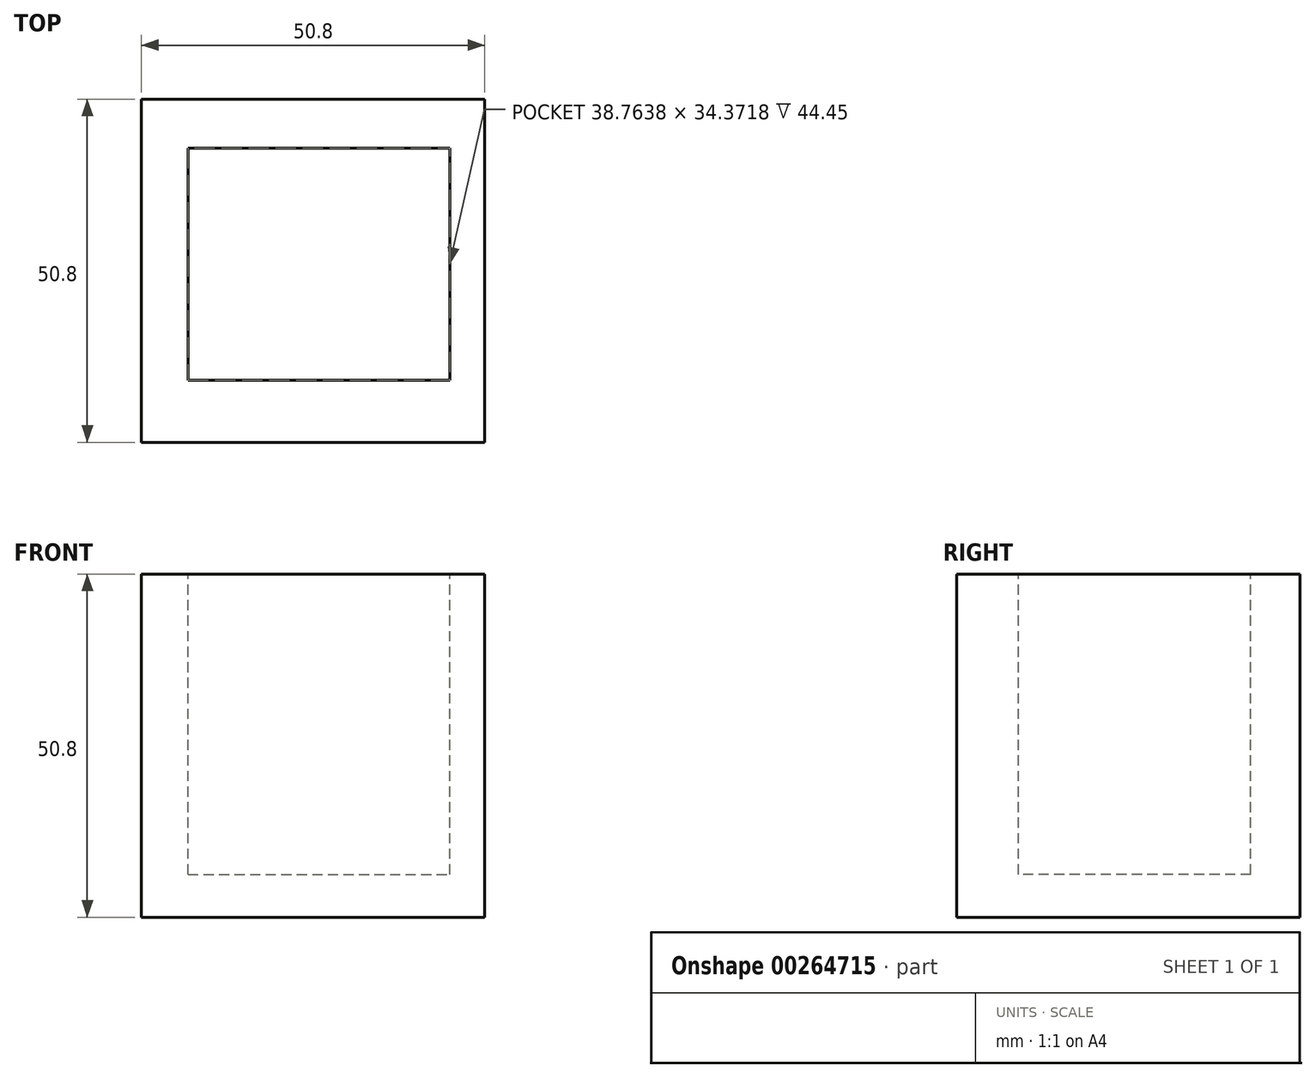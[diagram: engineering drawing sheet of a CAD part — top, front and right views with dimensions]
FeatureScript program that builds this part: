
annotation { "Feature Type Name" : "Feature", "Feature Type Description" : "" }
export const myFeature = defineFeature(function(context is Context, id is Id, definition is map)
    precondition{}
    {
        {
            var Q0;
            Q0=qCreatedBy(makeId("Front.planeOp"),FACE);
            var sketch = newSketch(context, id + "F0", { "sketchPlane" : qUnion([Q0])});
            skLineSegment(sketch, "E0.bottom", {"start": v(0, 0) * mm, "end": v(-50.8, 0) * mm});
            skLineSegment(sketch, "E0.top", {"start": v(0, 50.8) * mm, "end": v(-50.8, 50.8) * mm});
            skLineSegment(sketch, "E0.left", {"start": v(0, 0) * mm, "end": v(0, 50.8) * mm});
            skLineSegment(sketch, "E0.right", {"start": v(-50.8, 0) * mm, "end": v(-50.8, 50.8) * mm});
            skSolve(sketch);
        }
        {
            var Q0;
            Q0 = qSketchRegion(id + "F0", true);
            extrude(context, id + "F1", {"entities" : qUnion([Q0]), "depth" : 50.8 * mm});
        }
        {
            var Q0;
            Q0=makeQuery(id+"F1.opExtrude","SWEPT_FACE",FACE,{"disambiguationData":[OSD([sQuery(id+"F0.wireOp",EDGE,"E0.top")])]});
            var sketch = newSketch(context, id + "F2", { "sketchPlane" : qUnion([Q0])});
            skLineSegment(sketch, "E1.bottom", {"start": v(-43.92, -7.26) * mm, "end": v(-5.16, -7.26) * mm});
            skLineSegment(sketch, "E1.top", {"start": v(-43.92, -41.63) * mm, "end": v(-5.16, -41.63) * mm});
            skLineSegment(sketch, "E1.left", {"start": v(-43.92, -7.26) * mm, "end": v(-43.92, -41.63) * mm});
            skLineSegment(sketch, "E1.right", {"start": v(-5.16, -7.26) * mm, "end": v(-5.16, -41.63) * mm});
            skSolve(sketch);
        }
        {
            var Q0;
            Q0 = qSketchRegion(id + "F2", true);
            extrude(context, id + "F3", {"entities" : qUnion([Q0]), "operationType" : NewBodyOperationType.REMOVE, "oppositeDirection" : true, "depth" : 44.45 * mm});
        }
    });
